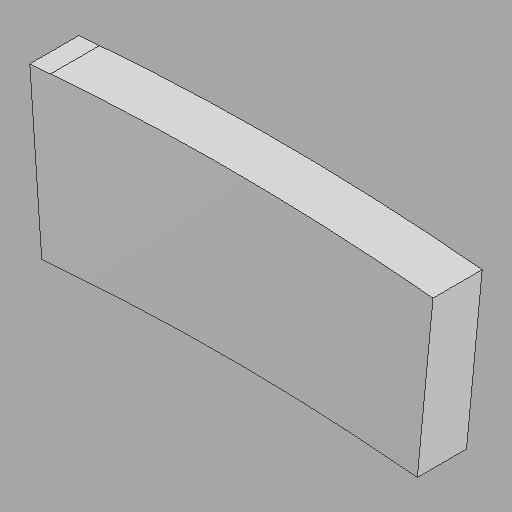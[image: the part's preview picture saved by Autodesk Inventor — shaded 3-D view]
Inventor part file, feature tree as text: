
AUTODESK INVENTOR PART (.ipt)
format: ipt  version: 2022.1 (Build 261234020, 234B)  size: 90,624 bytes
history: imported  units: in
note: dims shown in document units (in); Inventor stores cm internally (conversion verified against a paired STEP export)
features: imported_body x1
ambient origin geometry x8: Origin, YZ Plane, XZ Plane, XY Plane, X Axis, Y Axis, Z Axis, Center Point
bodies: Solid1 (imported_parasolid)
feature tree (1):
  imported_body  NMx_Import_Brep_tag  [imported B-rep: ~8 faces, bbox_mm=[1249.421707, 514.369354, 152.4]]
